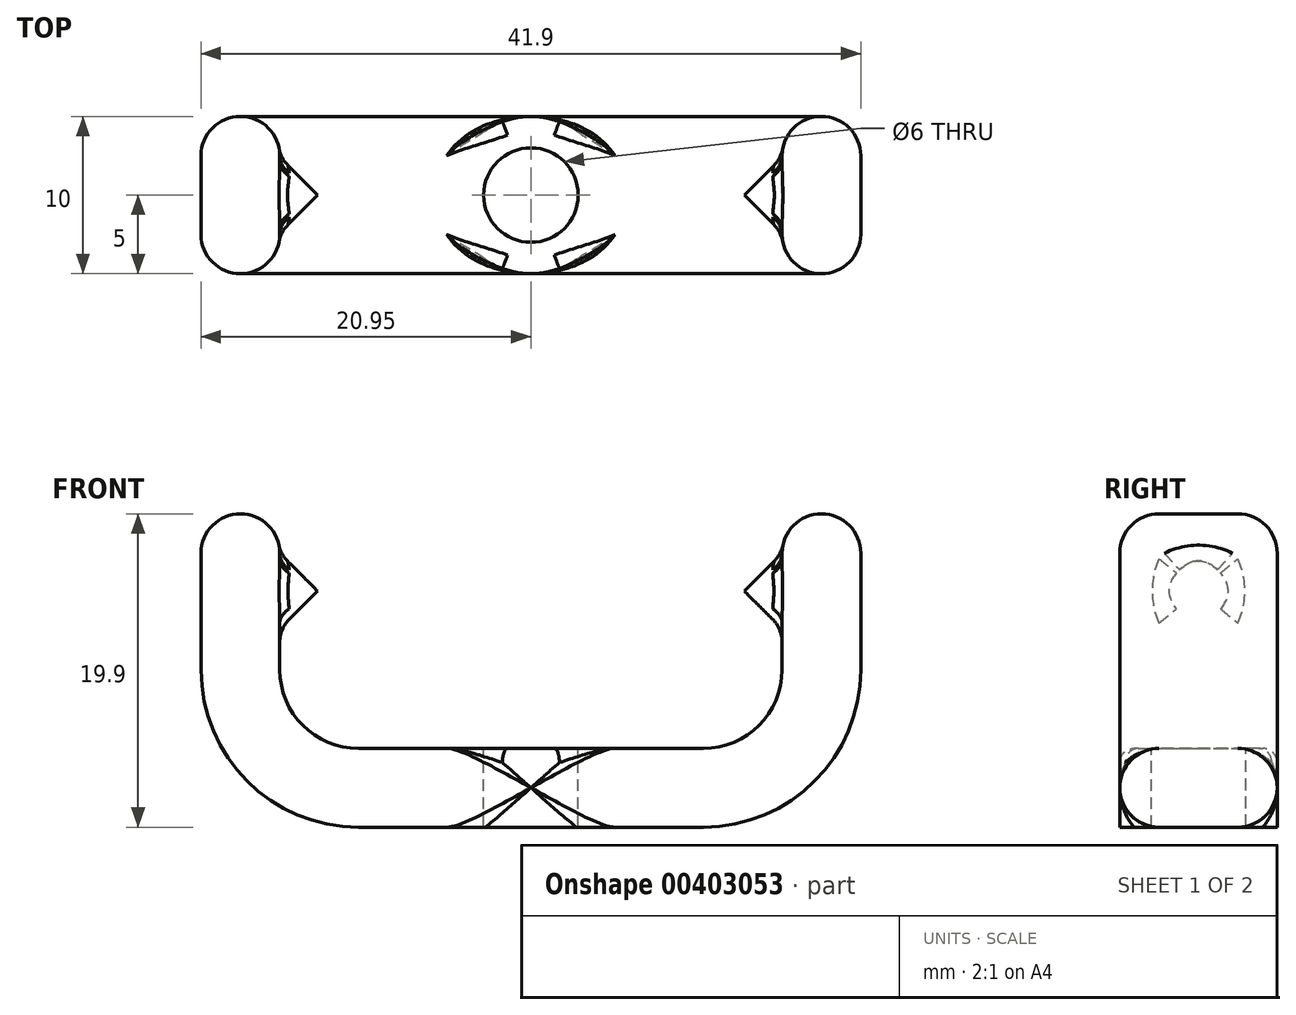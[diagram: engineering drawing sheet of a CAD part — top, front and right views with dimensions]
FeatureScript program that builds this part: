
annotation { "Feature Type Name" : "Feature", "Feature Type Description" : "" }
export const myFeature = defineFeature(function(context is Context, id is Id, definition is map)
    precondition{}
    {
        {
            var Q0;
            Q0=qCreatedBy(makeId("Front.planeOp"),FACE);
            var sketch = newSketch(context, id + "F0", { "sketchPlane" : qUnion([Q0])});
            skLineSegment(sketch, "E0", {"start": v(-15.95, 12.4) * mm, "end": v(-15.95, 5) * mm});
            skLineSegment(sketch, "E1", {"start": v(-10.95, 0) * mm, "end": v(0, 0) * mm});
            skPoint(sketch, "E2.visualSharp", {"position": v(-15.95, 0) * mm});
            skArc(sketch, "E2.filletArc", {"start": v(-15.95, 5) * mm, "mid": v(-14.49, 1.46) * mm, "end": v(-10.95, 0) * mm});
            skPoint(sketch, "E3.visualSharp", {"position": v(15.93, 0) * mm});
            skLineSegment(sketch, "E4.1", {"start": v(-20.95, 12.4) * mm, "end": v(-20.95, 5) * mm});
            skArc(sketch, "E4.2", {"start": v(-20.95, 5) * mm, "mid": v(-18.02, -2.07) * mm, "end": v(-10.95, -5) * mm});
            skLineSegment(sketch, "E4.3", {"start": v(-10.95, -5) * mm, "end": v(0, -5) * mm});
            skArc(sketch, "E5", {"start": v(-20.95, 12.4) * mm, "mid": v(-18.45, 14.9) * mm, "end": v(-15.95, 12.4) * mm});
            skLineSegment(sketch, "E6.MirrorCS", {"start": v(20.95, 12.4) * mm, "end": v(20.95, 5) * mm});
            skArc(sketch, "E7.MirrorCS", {"start": v(20.95, 12.4) * mm, "mid": v(18.45, 14.9) * mm, "end": v(15.95, 12.4) * mm});
            skLineSegment(sketch, "E8.MirrorCS", {"start": v(15.95, 12.4) * mm, "end": v(15.95, 5) * mm});
            skArc(sketch, "E9.MirrorCS", {"start": v(20.95, 5) * mm, "mid": v(18.02, -2.07) * mm, "end": v(10.95, -5) * mm});
            skArc(sketch, "E10.MirrorCS", {"start": v(15.95, 5) * mm, "mid": v(14.49, 1.46) * mm, "end": v(10.95, 0) * mm});
            skLineSegment(sketch, "E11.MirrorCS", {"start": v(10.95, 0) * mm, "end": v(0, 0) * mm});
            skLineSegment(sketch, "E12.MirrorCS", {"start": v(10.95, -5) * mm, "end": v(0, -5) * mm});
            skLineSegment(sketch, "E13", {"start": v(-15.95, 12.4) * mm, "end": v(-13.55, 10) * mm});
            skLineSegment(sketch, "E14", {"start": v(-13.55, 10) * mm, "end": v(-15.95, 10) * mm});
            skLineSegment(sketch, "E15.MirrorCS", {"start": v(15.95, 10) * mm, "end": v(13.55, 10) * mm});
            skLineSegment(sketch, "E16.MirrorCS", {"start": v(15.95, 12.4) * mm, "end": v(13.55, 10) * mm});
            skSolve(sketch);
        }
        {
            var Q0;
            Q0=makeQuery(id+"F0.imprint","IMPRINT",FACE,{"disambiguationData":[TD([[makeQuery(id+"F0.imprint","IMPRINT",EDGE,{"derivedFrom":sQuery(id+"F0.wireOp",EDGE,"E1")}),-1.0]])]});
            extrude(context, id + "F1", {"entities" : qUnion([Q0]), "depth" : 5 * mm, "hasSecondDirection" : true, "secondDirectionOppositeDirection" : true, "secondDirectionDepth" : 5 * mm});
        }
        {
            var Q0;
            {var subQ0=sQuery(id+"F0.wireOp",EDGE,"E13");Q0=makeQuery(id+"F0.imprint","IMPRINT",FACE,{"disambiguationData":[TD([[makeQuery(id+"F0.imprint","IMPRINT",EDGE,{"derivedFrom":subQ0}),-1.0]])]});}
            var Q1;
            {var subQ2=sQuery(id+"F0.wireOp",EDGE,"E15.MirrorCS");Q1=makeQuery(id+"F0.imprint","IMPRINT",FACE,{"disambiguationData":[TD([[makeQuery(id+"F0.imprint","IMPRINT",EDGE,{"derivedFrom":subQ2}),-1.0]])]});}
            var Q2;
            Q2=sQuery(id+"F0.wireOp",EDGE,"E14");
            revolve(context, id + "F2", {"operationType" : NewBodyOperationType.ADD, "entities" : qUnion([Q0, Q1]), "axis" : qUnion([Q2]), "revolveType" : RevolveType.FULL});
        }
        {
            var Q0;
            Q0=makeQuery(id+"F1.opExtrude","CAP_FACE",FACE,{"disambiguationData":[OSD([sQuery(id+"F0.wireOp",EDGE,"E0"),sQuery(id+"F0.wireOp",EDGE,"E1"),sQuery(id+"F0.wireOp",EDGE,"E2.filletArc"),sQuery(id+"F0.wireOp",EDGE,"E4.1"),sQuery(id+"F0.wireOp",EDGE,"E4.2"),sQuery(id+"F0.wireOp",EDGE,"E4.3"),sQuery(id+"F0.wireOp",EDGE,"E5"),sQuery(id+"F0.wireOp",EDGE,"E6.MirrorCS"),sQuery(id+"F0.wireOp",EDGE,"E7.MirrorCS"),sQuery(id+"F0.wireOp",EDGE,"E8.MirrorCS"),sQuery(id+"F0.wireOp",EDGE,"E9.MirrorCS"),sQuery(id+"F0.wireOp",EDGE,"E10.MirrorCS"),sQuery(id+"F0.wireOp",EDGE,"E11.MirrorCS"),sQuery(id+"F0.wireOp",EDGE,"E12.MirrorCS")])],"isStart":false});
            var Q1;
            Q1=makeQuery(id+"F1.opExtrude","CAP_FACE",FACE,{"disambiguationData":[OSD([sQuery(id+"F0.wireOp",EDGE,"E0"),sQuery(id+"F0.wireOp",EDGE,"E1"),sQuery(id+"F0.wireOp",EDGE,"E2.filletArc"),sQuery(id+"F0.wireOp",EDGE,"E4.1"),sQuery(id+"F0.wireOp",EDGE,"E4.2"),sQuery(id+"F0.wireOp",EDGE,"E4.3"),sQuery(id+"F0.wireOp",EDGE,"E5"),sQuery(id+"F0.wireOp",EDGE,"E6.MirrorCS"),sQuery(id+"F0.wireOp",EDGE,"E7.MirrorCS"),sQuery(id+"F0.wireOp",EDGE,"E8.MirrorCS"),sQuery(id+"F0.wireOp",EDGE,"E9.MirrorCS"),sQuery(id+"F0.wireOp",EDGE,"E10.MirrorCS"),sQuery(id+"F0.wireOp",EDGE,"E11.MirrorCS"),sQuery(id+"F0.wireOp",EDGE,"E12.MirrorCS")])],"isStart":true});
            fillet(context, id + "F3", {"entities" : qUnion([Q0, Q1]), "radius" : 2.5 * mm, "tangentPropagation" : true, "allowEdgeOverflow" : false});
        }
        {
            var Q0;
            Q0=makeQuery(id+"F1.opExtrude","SWEPT_FACE",FACE,{"disambiguationData":[OSD([sQuery(id+"F0.wireOp",EDGE,"E1"),sQuery(id+"F0.wireOp",EDGE,"E11.MirrorCS")])]});
            var sketch = newSketch(context, id + "F4", { "sketchPlane" : qUnion([Q0])});
            skCircle(sketch, "E17", {"center": v(0, 0) * mm, "radius": 3 * mm});
            skCircle(sketch, "E18", {"center": v(0, 0) * mm, "radius": 5 * mm});
            skLineSegment(sketch, "E19", {"start": v(10.95, -5) * mm, "end": v(-10.95, -5) * mm, "construction": true});
            skSolve(sketch);
        }
        {
            var Q0;
            {var subQ0=sQuery(id+"F4.wireOp",EDGE,"E17");var subQ1=sQuery(id+"F0.wireOp",EDGE,"E11.MirrorCS");var subQ2=sQuery(id+"F0.wireOp",EDGE,"E1");var subQ3=makeQuery(id+"F3.opFillet","BLEND_EDGE",EDGE,{"blendedFrom":[makeQuery(id+"F1.opExtrude","CAP_EDGE",EDGE,{"disambiguationData":[OSD([subQ2,subQ1])],"isStart":true}),makeQuery(id+"F1.opExtrude","SWEPT_FACE",FACE,{"disambiguationData":[OSD([subQ2,subQ1])]})],"blendedInto":[makeQuery(id+"F1.opExtrude","SWEPT_FACE",FACE,{"disambiguationData":[OSD([subQ2,subQ1])]})]});var subQ4=makeQuery(id+"F4.imprint","INTERSECT",VERTEX,{"disambiguationData":[OD(0.0)],"derivedFrom":[subQ3,subQ0]});Q0=makeQuery(id+"F4.imprint","IMPRINT",FACE,{"disambiguationData":[TD([[makeQuery(id+"F4.imprint","IMPRINT",EDGE,{"disambiguationData":[TD([[subQ4,1.0]])],"derivedFrom":subQ0}),-1.0]])]});}
            var Q1;
            {var subQ0=sQuery(id+"F4.wireOp",EDGE,"E17");var subQ1=sQuery(id+"F0.wireOp",EDGE,"E11.MirrorCS");var subQ2=sQuery(id+"F0.wireOp",EDGE,"E1");var subQ3=makeQuery(id+"F1.opExtrude","SWEPT_FACE",FACE,{"disambiguationData":[OSD([subQ2,subQ1])]});var subQ4=makeQuery(id+"F3.opFillet","BLEND_EDGE",EDGE,{"blendedFrom":[makeQuery(id+"F1.opExtrude","CAP_EDGE",EDGE,{"disambiguationData":[OSD([subQ2,subQ1])],"isStart":true}),subQ3],"blendedInto":[subQ3]});var subQ5=makeQuery(id+"F4.imprint","INTERSECT",VERTEX,{"disambiguationData":[OD(1.0)],"derivedFrom":[subQ4,subQ0]});Q1=makeQuery(id+"F4.imprint","IMPRINT",FACE,{"disambiguationData":[TD([[makeQuery(id+"F4.imprint","IMPRINT",EDGE,{"disambiguationData":[TD([[subQ5,1.0]])],"derivedFrom":subQ0}),-1.0]])]});}
            var Q2;
            {var subQ0=sQuery(id+"F4.wireOp",EDGE,"E17");var subQ1=sQuery(id+"F0.wireOp",EDGE,"E11.MirrorCS");var subQ2=sQuery(id+"F0.wireOp",EDGE,"E1");var subQ3=makeQuery(id+"F3.opFillet","BLEND_EDGE",EDGE,{"blendedFrom":[makeQuery(id+"F1.opExtrude","CAP_EDGE",EDGE,{"disambiguationData":[OSD([subQ2,subQ1])],"isStart":false}),makeQuery(id+"F1.opExtrude","SWEPT_FACE",FACE,{"disambiguationData":[OSD([subQ2,subQ1])]})],"blendedInto":[makeQuery(id+"F1.opExtrude","SWEPT_FACE",FACE,{"disambiguationData":[OSD([subQ2,subQ1])]})]});var subQ4=makeQuery(id+"F4.imprint","INTERSECT",VERTEX,{"disambiguationData":[OD(0.0)],"derivedFrom":[subQ3,subQ0]});Q2=makeQuery(id+"F4.imprint","IMPRINT",FACE,{"disambiguationData":[TD([[makeQuery(id+"F4.imprint","IMPRINT",EDGE,{"disambiguationData":[TD([[subQ4,-1.0]])],"derivedFrom":subQ0}),-1.0]])]});}
            var Q3;
            {var subQ0=sQuery(id+"F4.wireOp",EDGE,"E17");var subQ1=sQuery(id+"F0.wireOp",EDGE,"E11.MirrorCS");var subQ2=sQuery(id+"F0.wireOp",EDGE,"E1");var subQ3=makeQuery(id+"F1.opExtrude","SWEPT_FACE",FACE,{"disambiguationData":[OSD([subQ2,subQ1])]});var subQ4=makeQuery(id+"F3.opFillet","BLEND_EDGE",EDGE,{"blendedFrom":[makeQuery(id+"F1.opExtrude","CAP_EDGE",EDGE,{"disambiguationData":[OSD([subQ2,subQ1])],"isStart":true}),subQ3],"blendedInto":[subQ3]});var subQ5=makeQuery(id+"F4.imprint","INTERSECT",VERTEX,{"disambiguationData":[OD(0.0)],"derivedFrom":[subQ4,subQ0]});Q3=makeQuery(id+"F4.imprint","IMPRINT",FACE,{"disambiguationData":[TD([[makeQuery(id+"F4.imprint","IMPRINT",EDGE,{"disambiguationData":[TD([[subQ5,-1.0]])],"derivedFrom":subQ0}),-1.0]])]});}
            var Q4;
            Q4=makeQuery(id+"F1.opExtrude","SWEPT_FACE",FACE,{"disambiguationData":[OSD([sQuery(id+"F0.wireOp",EDGE,"E4.3"),sQuery(id+"F0.wireOp",EDGE,"E12.MirrorCS")])]});
            extrude(context, id + "F5", {"entities" : qUnion([Q0, Q1, Q2, Q3]), "operationType" : NewBodyOperationType.ADD, "endBound" : BoundingType.UP_TO_SURFACE, "oppositeDirection" : true, "endBoundEntityFace" : qUnion([Q4]), "depth" : 25 * mm});
        }
        {
            var Q0;
            {var subQ0=sQuery(id+"F4.wireOp",EDGE,"E17");var subQ1=sQuery(id+"F0.wireOp",EDGE,"E11.MirrorCS");var subQ2=sQuery(id+"F0.wireOp",EDGE,"E1");var subQ3=makeQuery(id+"F1.opExtrude","SWEPT_FACE",FACE,{"disambiguationData":[OSD([subQ2,subQ1])]});var subQ4=makeQuery(id+"F3.opFillet","BLEND_EDGE",EDGE,{"blendedFrom":[makeQuery(id+"F1.opExtrude","CAP_EDGE",EDGE,{"disambiguationData":[OSD([subQ2,subQ1])],"isStart":true}),subQ3],"blendedInto":[subQ3]});var subQ5=makeQuery(id+"F4.imprint","INTERSECT",VERTEX,{"disambiguationData":[OD(0.0)],"derivedFrom":[subQ4,subQ0]});Q0=makeQuery(id+"F4.imprint","IMPRINT",FACE,{"disambiguationData":[TD([[makeQuery(id+"F4.imprint","IMPRINT",EDGE,{"disambiguationData":[TD([[subQ5,-1.0]])],"derivedFrom":subQ0}),1.0]])]});}
            var Q1;
            {var subQ0=sQuery(id+"F4.wireOp",EDGE,"E17");var subQ1=sQuery(id+"F0.wireOp",EDGE,"E11.MirrorCS");var subQ2=sQuery(id+"F0.wireOp",EDGE,"E1");var subQ3=makeQuery(id+"F3.opFillet","BLEND_EDGE",EDGE,{"blendedFrom":[makeQuery(id+"F1.opExtrude","CAP_EDGE",EDGE,{"disambiguationData":[OSD([subQ2,subQ1])],"isStart":false}),makeQuery(id+"F1.opExtrude","SWEPT_FACE",FACE,{"disambiguationData":[OSD([subQ2,subQ1])]})],"blendedInto":[makeQuery(id+"F1.opExtrude","SWEPT_FACE",FACE,{"disambiguationData":[OSD([subQ2,subQ1])]})]});var subQ4=makeQuery(id+"F4.imprint","INTERSECT",VERTEX,{"disambiguationData":[OD(0.0)],"derivedFrom":[subQ3,subQ0]});Q1=makeQuery(id+"F4.imprint","IMPRINT",FACE,{"disambiguationData":[TD([[makeQuery(id+"F4.imprint","IMPRINT",EDGE,{"disambiguationData":[TD([[subQ4,-1.0]])],"derivedFrom":subQ0}),1.0]])]});}
            var Q2;
            {var subQ0=sQuery(id+"F4.wireOp",EDGE,"E17");var subQ1=sQuery(id+"F0.wireOp",EDGE,"E11.MirrorCS");var subQ2=sQuery(id+"F0.wireOp",EDGE,"E1");var subQ3=makeQuery(id+"F3.opFillet","BLEND_EDGE",EDGE,{"blendedFrom":[makeQuery(id+"F1.opExtrude","CAP_EDGE",EDGE,{"disambiguationData":[OSD([subQ2,subQ1])],"isStart":true}),makeQuery(id+"F1.opExtrude","SWEPT_FACE",FACE,{"disambiguationData":[OSD([subQ2,subQ1])]})],"blendedInto":[makeQuery(id+"F1.opExtrude","SWEPT_FACE",FACE,{"disambiguationData":[OSD([subQ2,subQ1])]})]});var subQ4=makeQuery(id+"F4.imprint","INTERSECT",VERTEX,{"disambiguationData":[OD(0.0)],"derivedFrom":[subQ3,subQ0]});Q2=makeQuery(id+"F4.imprint","IMPRINT",FACE,{"disambiguationData":[TD([[makeQuery(id+"F4.imprint","IMPRINT",EDGE,{"disambiguationData":[TD([[subQ4,1.0]])],"derivedFrom":subQ0}),1.0]])]});}
            extrude(context, id + "F6", {"entities" : qUnion([Q0, Q1, Q2]), "operationType" : NewBodyOperationType.REMOVE, "endBound" : BoundingType.THROUGH_ALL, "oppositeDirection" : true, "depth" : 25 * mm});
        }
        {
            var Q0;
            {var subQ0=sQuery(id+"F0.wireOp",EDGE,"E11.MirrorCS");var subQ1=sQuery(id+"F0.wireOp",EDGE,"E1");var subQ2=sQuery(id+"F4.wireOp",EDGE,"E18");Q0=makeQuery(id+"F5.boolean.opBoolean","SPLIT",EDGE,{"disambiguationData":[TD([makeQuery(id+"F3.opFillet","BLEND_FACE",FACE,{"disambiguationData":[OSD([subQ1,subQ0]),TDD([makeQuery(id+"F1.opExtrude","CAP_EDGE",EDGE,{"disambiguationData":[OSD([subQ1,subQ0])],"isStart":false})])]})])],"derivedFrom":makeQuery(id+"F5.opExtrude","CAP_EDGE",EDGE,{"disambiguationData":[OSD([subQ2])],"isStart":true})});}
            var Q1;
            {var subQ0=sQuery(id+"F0.wireOp",EDGE,"E11.MirrorCS");var subQ1=sQuery(id+"F0.wireOp",EDGE,"E1");var subQ2=sQuery(id+"F4.wireOp",EDGE,"E18");Q1=makeQuery(id+"F5.boolean.opBoolean","SPLIT",EDGE,{"disambiguationData":[TD([makeQuery(id+"F3.opFillet","BLEND_FACE",FACE,{"disambiguationData":[OSD([subQ1,subQ0]),TDD([makeQuery(id+"F1.opExtrude","CAP_EDGE",EDGE,{"disambiguationData":[OSD([subQ1,subQ0])],"isStart":true})])]})])],"derivedFrom":makeQuery(id+"F5.opExtrude","CAP_EDGE",EDGE,{"disambiguationData":[OSD([subQ2])],"isStart":true})});}
            var Q2;
            {var subQ0=sQuery(id+"F0.wireOp",EDGE,"E12.MirrorCS");var subQ1=sQuery(id+"F0.wireOp",EDGE,"E4.3");var subQ2=makeQuery(id+"F1.opExtrude","SWEPT_FACE",FACE,{"disambiguationData":[OSD([subQ1,subQ0])]});var subQ3=sQuery(id+"F0.wireOp",EDGE,"E11.MirrorCS");var subQ4=sQuery(id+"F0.wireOp",EDGE,"E1");var subQ5=makeQuery(id+"F1.opExtrude","CAP_EDGE",EDGE,{"disambiguationData":[OSD([subQ4,subQ3])],"isStart":true});var subQ6=sQuery(id+"F4.wireOp",EDGE,"E18");var subQ7=makeQuery(id+"F1.opExtrude","SWEPT_FACE",FACE,{"disambiguationData":[OSD([subQ4,subQ3])]});var subQ8=makeQuery(id+"F3.opFillet","BLEND_EDGE",EDGE,{"blendedFrom":[subQ5,subQ7],"blendedInto":[subQ7]});var subQ9=makeQuery(id+"F4.imprint","INTERSECT",VERTEX,{"disambiguationData":[OD(1.0)],"derivedFrom":[subQ8,subQ6]});var subQ10=makeQuery(id+"F3.opFillet","BLEND_EDGE",EDGE,{"blendedFrom":[makeQuery(id+"F1.opExtrude","CAP_EDGE",EDGE,{"disambiguationData":[OSD([subQ4,subQ3])],"isStart":false}),subQ7],"blendedInto":[subQ7]});var subQ12=makeQuery(id+"F4.imprint","INTERSECT",VERTEX,{"disambiguationData":[OD(0.0)],"derivedFrom":[subQ10,subQ6]});var subQ13=makeQuery(id+"F4.imprint","INTERSECT",VERTEX,{"disambiguationData":[OD(0.0)],"derivedFrom":[subQ8,subQ6]});Q2=makeQuery(id+"F5.boolean.opBoolean","SPLIT",EDGE,{"disambiguationData":[TD([makeQuery(id+"F3.opFillet","BLEND_FACE",FACE,{"disambiguationData":[OSD([subQ4,subQ3]),TDD([subQ5])]})])],"derivedFrom":makeQuery(id+"F5.opExtrude","TWEAK_EDGE",EDGE,{"derivedFrom":[subQ2,makeQuery(id+"F4.imprint","IMPRINT",EDGE,{"disambiguationData":[TD([[subQ13,1.0]])],"derivedFrom":subQ6}),makeQuery(id+"F4.imprint","IMPRINT",EDGE,{"disambiguationData":[TD([[subQ13,-1.0]])],"derivedFrom":subQ6}),makeQuery(id+"F4.imprint","IMPRINT",EDGE,{"disambiguationData":[TD([[subQ12,-1.0]])],"derivedFrom":subQ6}),makeQuery(id+"F4.imprint","IMPRINT",EDGE,{"disambiguationData":[TD([[subQ9,1.0]])],"derivedFrom":subQ6})]})});}
            var Q3;
            {var subQ0=sQuery(id+"F0.wireOp",EDGE,"E12.MirrorCS");var subQ1=sQuery(id+"F0.wireOp",EDGE,"E4.3");var subQ2=makeQuery(id+"F1.opExtrude","SWEPT_FACE",FACE,{"disambiguationData":[OSD([subQ1,subQ0])]});var subQ3=sQuery(id+"F0.wireOp",EDGE,"E11.MirrorCS");var subQ4=sQuery(id+"F0.wireOp",EDGE,"E1");var subQ5=makeQuery(id+"F1.opExtrude","CAP_EDGE",EDGE,{"disambiguationData":[OSD([subQ4,subQ3])],"isStart":false});var subQ6=sQuery(id+"F4.wireOp",EDGE,"E18");var subQ7=makeQuery(id+"F1.opExtrude","SWEPT_FACE",FACE,{"disambiguationData":[OSD([subQ4,subQ3])]});var subQ8=makeQuery(id+"F3.opFillet","BLEND_EDGE",EDGE,{"blendedFrom":[makeQuery(id+"F1.opExtrude","CAP_EDGE",EDGE,{"disambiguationData":[OSD([subQ4,subQ3])],"isStart":true}),subQ7],"blendedInto":[subQ7]});var subQ9=makeQuery(id+"F4.imprint","INTERSECT",VERTEX,{"disambiguationData":[OD(1.0)],"derivedFrom":[subQ8,subQ6]});var subQ10=makeQuery(id+"F3.opFillet","BLEND_EDGE",EDGE,{"blendedFrom":[subQ5,subQ7],"blendedInto":[subQ7]});var subQ12=makeQuery(id+"F4.imprint","INTERSECT",VERTEX,{"disambiguationData":[OD(0.0)],"derivedFrom":[subQ10,subQ6]});var subQ13=makeQuery(id+"F4.imprint","INTERSECT",VERTEX,{"disambiguationData":[OD(0.0)],"derivedFrom":[subQ8,subQ6]});Q3=makeQuery(id+"F5.boolean.opBoolean","SPLIT",EDGE,{"disambiguationData":[TD([makeQuery(id+"F3.opFillet","BLEND_FACE",FACE,{"disambiguationData":[OSD([subQ4,subQ3]),TDD([subQ5])]})])],"derivedFrom":makeQuery(id+"F5.opExtrude","TWEAK_EDGE",EDGE,{"derivedFrom":[subQ2,makeQuery(id+"F4.imprint","IMPRINT",EDGE,{"disambiguationData":[TD([[subQ13,1.0]])],"derivedFrom":subQ6}),makeQuery(id+"F4.imprint","IMPRINT",EDGE,{"disambiguationData":[TD([[subQ13,-1.0]])],"derivedFrom":subQ6}),makeQuery(id+"F4.imprint","IMPRINT",EDGE,{"disambiguationData":[TD([[subQ12,-1.0]])],"derivedFrom":subQ6}),makeQuery(id+"F4.imprint","IMPRINT",EDGE,{"disambiguationData":[TD([[subQ9,1.0]])],"derivedFrom":subQ6})]})});}
            var Q4;
            {var subQ0=sQuery(id+"F0.wireOp",EDGE,"E12.MirrorCS");var subQ1=sQuery(id+"F0.wireOp",EDGE,"E4.3");var subQ2=makeQuery(id+"F1.opExtrude","SWEPT_FACE",FACE,{"disambiguationData":[OSD([subQ1,subQ0])]});var subQ3=sQuery(id+"F4.wireOp",EDGE,"E17");var subQ5=sQuery(id+"F0.wireOp",EDGE,"E11.MirrorCS");var subQ6=sQuery(id+"F0.wireOp",EDGE,"E1");var subQ7=makeQuery(id+"F1.opExtrude","CAP_EDGE",EDGE,{"disambiguationData":[OSD([subQ6,subQ5])],"isStart":false});var subQ9=makeQuery(id+"F1.opExtrude","SWEPT_FACE",FACE,{"disambiguationData":[OSD([subQ6,subQ5])]});var subQ10=makeQuery(id+"F1.opExtrude","CAP_EDGE",EDGE,{"disambiguationData":[OSD([subQ6,subQ5])],"isStart":true});var subQ11=makeQuery(id+"F3.opFillet","BLEND_EDGE",EDGE,{"blendedFrom":[subQ10,subQ9],"blendedInto":[subQ9]});var subQ12=makeQuery(id+"F4.imprint","INTERSECT",VERTEX,{"disambiguationData":[OD(1.0)],"derivedFrom":[subQ11,subQ3]});var subQ13=makeQuery(id+"F3.opFillet","BLEND_EDGE",EDGE,{"blendedFrom":[subQ7,subQ9],"blendedInto":[subQ9]});var subQ15=makeQuery(id+"F4.imprint","INTERSECT",VERTEX,{"disambiguationData":[OD(0.0)],"derivedFrom":[subQ13,subQ3]});var subQ16=makeQuery(id+"F4.imprint","INTERSECT",VERTEX,{"disambiguationData":[OD(0.0)],"derivedFrom":[subQ11,subQ3]});var subQ17=makeQuery(id+"F5.opExtrude","TWEAK_EDGE",EDGE,{"derivedFrom":[subQ2,makeQuery(id+"F4.imprint","IMPRINT",EDGE,{"disambiguationData":[TD([[subQ16,1.0]])],"derivedFrom":subQ3}),makeQuery(id+"F4.imprint","IMPRINT",EDGE,{"disambiguationData":[TD([[subQ16,-1.0]])],"derivedFrom":subQ3}),makeQuery(id+"F4.imprint","IMPRINT",EDGE,{"disambiguationData":[TD([[subQ15,-1.0]])],"derivedFrom":subQ3}),makeQuery(id+"F4.imprint","IMPRINT",EDGE,{"disambiguationData":[TD([[subQ12,1.0]])],"derivedFrom":subQ3})]});Q4=makeQuery(id+"F6.boolean.opBoolean","MERGE",EDGE,{"derivedFrom":[makeQuery(id+"F5.boolean.opBoolean","SPLIT",EDGE,{"disambiguationData":[TD([makeQuery(id+"F3.opFillet","BLEND_FACE",FACE,{"disambiguationData":[OSD([subQ6,subQ5]),TDD([subQ10])]})])],"derivedFrom":subQ17}),makeQuery(id+"F5.boolean.opBoolean","SPLIT",EDGE,{"disambiguationData":[TD([makeQuery(id+"F3.opFillet","BLEND_FACE",FACE,{"disambiguationData":[OSD([subQ6,subQ5]),TDD([subQ7])]})])],"derivedFrom":subQ17})]});}
            var Q5;
            {var subQ0=sQuery(id+"F4.wireOp",EDGE,"E17");var subQ1=sQuery(id+"F0.wireOp",EDGE,"E11.MirrorCS");var subQ2=sQuery(id+"F0.wireOp",EDGE,"E1");var subQ6=makeQuery(id+"F5.opExtrude","CAP_EDGE",EDGE,{"disambiguationData":[OSD([subQ0])],"isStart":true});Q5=makeQuery(id+"F6.boolean.opBoolean","MERGE",EDGE,{"derivedFrom":[makeQuery(id+"F5.boolean.opBoolean","SPLIT",EDGE,{"disambiguationData":[TD([makeQuery(id+"F3.opFillet","BLEND_FACE",FACE,{"disambiguationData":[OSD([subQ2,subQ1]),TDD([makeQuery(id+"F1.opExtrude","CAP_EDGE",EDGE,{"disambiguationData":[OSD([subQ2,subQ1])],"isStart":true})])]})])],"derivedFrom":subQ6}),makeQuery(id+"F5.boolean.opBoolean","SPLIT",EDGE,{"disambiguationData":[TD([makeQuery(id+"F3.opFillet","BLEND_FACE",FACE,{"disambiguationData":[OSD([subQ2,subQ1]),TDD([makeQuery(id+"F1.opExtrude","CAP_EDGE",EDGE,{"disambiguationData":[OSD([subQ2,subQ1])],"isStart":false})])]})])],"derivedFrom":subQ6}),makeQuery(id+"F6.opExtrude","CAP_EDGE",EDGE,{"disambiguationData":[OSD([subQ0])],"isStart":true})]});}
            var Q6;
            {var subQ0=sQuery(id+"F0.wireOp",EDGE,"E11.MirrorCS");var subQ1=sQuery(id+"F0.wireOp",EDGE,"E1");Q6=makeQuery(id+"F5.boolean.opBoolean","INTERSECT",EDGE,{"disambiguationData":[OD(2.0)],"derivedFrom":[makeQuery(id+"F3.opFillet","BLEND_FACE",FACE,{"disambiguationData":[OSD([subQ1,subQ0]),TDD([makeQuery(id+"F1.opExtrude","CAP_EDGE",EDGE,{"disambiguationData":[OSD([subQ1,subQ0])],"isStart":false})])]}),makeQuery(id+"F5.opExtrude","SWEPT_FACE",FACE,{"disambiguationData":[OSD([sQuery(id+"F4.wireOp",EDGE,"E18")])]})]});}
            var Q7;
            {var subQ0=sQuery(id+"F0.wireOp",EDGE,"E11.MirrorCS");var subQ1=sQuery(id+"F0.wireOp",EDGE,"E1");Q7=makeQuery(id+"F5.boolean.opBoolean","INTERSECT",EDGE,{"disambiguationData":[OD(1.0)],"derivedFrom":[makeQuery(id+"F3.opFillet","BLEND_FACE",FACE,{"disambiguationData":[OSD([subQ1,subQ0]),TDD([makeQuery(id+"F1.opExtrude","CAP_EDGE",EDGE,{"disambiguationData":[OSD([subQ1,subQ0])],"isStart":false})])]}),makeQuery(id+"F5.opExtrude","SWEPT_FACE",FACE,{"disambiguationData":[OSD([sQuery(id+"F4.wireOp",EDGE,"E18")])]})]});}
            var Q8;
            {var subQ0=sQuery(id+"F0.wireOp",EDGE,"E11.MirrorCS");var subQ1=sQuery(id+"F0.wireOp",EDGE,"E1");Q8=makeQuery(id+"F5.boolean.opBoolean","INTERSECT",EDGE,{"disambiguationData":[OD(0.0)],"derivedFrom":[makeQuery(id+"F3.opFillet","BLEND_FACE",FACE,{"disambiguationData":[OSD([subQ1,subQ0]),TDD([makeQuery(id+"F1.opExtrude","CAP_EDGE",EDGE,{"disambiguationData":[OSD([subQ1,subQ0])],"isStart":false})])]}),makeQuery(id+"F5.opExtrude","SWEPT_FACE",FACE,{"disambiguationData":[OSD([sQuery(id+"F4.wireOp",EDGE,"E18")])]})]});}
            var Q9;
            {var subQ0=sQuery(id+"F0.wireOp",EDGE,"E11.MirrorCS");var subQ1=sQuery(id+"F0.wireOp",EDGE,"E1");Q9=makeQuery(id+"F5.boolean.opBoolean","INTERSECT",EDGE,{"disambiguationData":[OD(3.0)],"derivedFrom":[makeQuery(id+"F3.opFillet","BLEND_FACE",FACE,{"disambiguationData":[OSD([subQ1,subQ0]),TDD([makeQuery(id+"F1.opExtrude","CAP_EDGE",EDGE,{"disambiguationData":[OSD([subQ1,subQ0])],"isStart":false})])]}),makeQuery(id+"F5.opExtrude","SWEPT_FACE",FACE,{"disambiguationData":[OSD([sQuery(id+"F4.wireOp",EDGE,"E18")])]})]});}
            var Q10;
            {var subQ0=sQuery(id+"F0.wireOp",EDGE,"E11.MirrorCS");var subQ1=sQuery(id+"F0.wireOp",EDGE,"E1");Q10=makeQuery(id+"F5.boolean.opBoolean","INTERSECT",EDGE,{"disambiguationData":[OD(0.0)],"derivedFrom":[makeQuery(id+"F3.opFillet","BLEND_FACE",FACE,{"disambiguationData":[OSD([subQ1,subQ0]),TDD([makeQuery(id+"F1.opExtrude","CAP_EDGE",EDGE,{"disambiguationData":[OSD([subQ1,subQ0])],"isStart":true})])]}),makeQuery(id+"F5.opExtrude","SWEPT_FACE",FACE,{"disambiguationData":[OSD([sQuery(id+"F4.wireOp",EDGE,"E18")])]})]});}
            var Q11;
            {var subQ0=sQuery(id+"F0.wireOp",EDGE,"E11.MirrorCS");var subQ1=sQuery(id+"F0.wireOp",EDGE,"E1");Q11=makeQuery(id+"F5.boolean.opBoolean","INTERSECT",EDGE,{"disambiguationData":[OD(3.0)],"derivedFrom":[makeQuery(id+"F3.opFillet","BLEND_FACE",FACE,{"disambiguationData":[OSD([subQ1,subQ0]),TDD([makeQuery(id+"F1.opExtrude","CAP_EDGE",EDGE,{"disambiguationData":[OSD([subQ1,subQ0])],"isStart":true})])]}),makeQuery(id+"F5.opExtrude","SWEPT_FACE",FACE,{"disambiguationData":[OSD([sQuery(id+"F4.wireOp",EDGE,"E18")])]})]});}
            var Q12;
            {var subQ0=sQuery(id+"F0.wireOp",EDGE,"E11.MirrorCS");var subQ1=sQuery(id+"F0.wireOp",EDGE,"E1");Q12=makeQuery(id+"F5.boolean.opBoolean","INTERSECT",EDGE,{"disambiguationData":[OD(2.0)],"derivedFrom":[makeQuery(id+"F3.opFillet","BLEND_FACE",FACE,{"disambiguationData":[OSD([subQ1,subQ0]),TDD([makeQuery(id+"F1.opExtrude","CAP_EDGE",EDGE,{"disambiguationData":[OSD([subQ1,subQ0])],"isStart":true})])]}),makeQuery(id+"F5.opExtrude","SWEPT_FACE",FACE,{"disambiguationData":[OSD([sQuery(id+"F4.wireOp",EDGE,"E18")])]})]});}
            var Q13;
            {var subQ0=sQuery(id+"F0.wireOp",EDGE,"E11.MirrorCS");var subQ1=sQuery(id+"F0.wireOp",EDGE,"E1");Q13=makeQuery(id+"F5.boolean.opBoolean","INTERSECT",EDGE,{"disambiguationData":[OD(1.0)],"derivedFrom":[makeQuery(id+"F3.opFillet","BLEND_FACE",FACE,{"disambiguationData":[OSD([subQ1,subQ0]),TDD([makeQuery(id+"F1.opExtrude","CAP_EDGE",EDGE,{"disambiguationData":[OSD([subQ1,subQ0])],"isStart":true})])]}),makeQuery(id+"F5.opExtrude","SWEPT_FACE",FACE,{"disambiguationData":[OSD([sQuery(id+"F4.wireOp",EDGE,"E18")])]})]});}
            fillet(context, id + "F7", {"entities" : qUnion([Q0, Q1, Q2, Q3, Q4, Q5, Q6, Q7, Q8, Q9, Q10, Q11, Q12, Q13]), "radius" : 0.9 * mm, "tangentPropagation" : true, "allowEdgeOverflow" : false});
        }
        {
            var Q0;
            Q0=makeQuery(id+"F2.opRevolve","SWEPT_FACE",FACE,{"disambiguationData":[OSD([sQuery(id+"F0.wireOp",EDGE,"E16.MirrorCS")])]});
            var Q1;
            Q1=makeQuery(id+"F2.opRevolve","SWEPT_FACE",FACE,{"disambiguationData":[OSD([sQuery(id+"F0.wireOp",EDGE,"E13")])]});
            fillet(context, id + "F8", {"entities" : qUnion([Q0, Q1]), "radius" : 2 * mm, "tangentPropagation" : true, "allowEdgeOverflow" : false});
        }
    });
